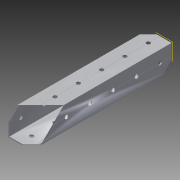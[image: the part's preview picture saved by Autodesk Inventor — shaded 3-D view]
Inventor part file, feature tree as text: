
AUTODESK INVENTOR PART (.ipt)
format: ipt  version: 2014 (Build 180170000, 170)  size: 1,175,040 bytes
history: native  units: in
note: dims shown in document units (in); Inventor stores cm internally (conversion verified against a paired STEP export)
features: pattern_circular x1, other x1, plane x1, extrude x1, imported_body x1, sketch x1
ambient origin geometry x8: Origin, YZ Plane, XZ Plane, XY Plane, X Axis, Y Axis, Z Axis, Center Point
bodies: Body1 (feature_tree)
feature tree (6):
  pattern_circular  "CirPattern2"
  other  "217-3426-STEP1"
  plane  "Work Plane1"
  extrude  "Extrusion1"  Depth=3937.0079in TaperAngle=0.0deg
  imported_body  "Base1"
  sketch  "Sketch1"  dims[d0=-7.0in d1=3937.0079in d2=0.0in]
